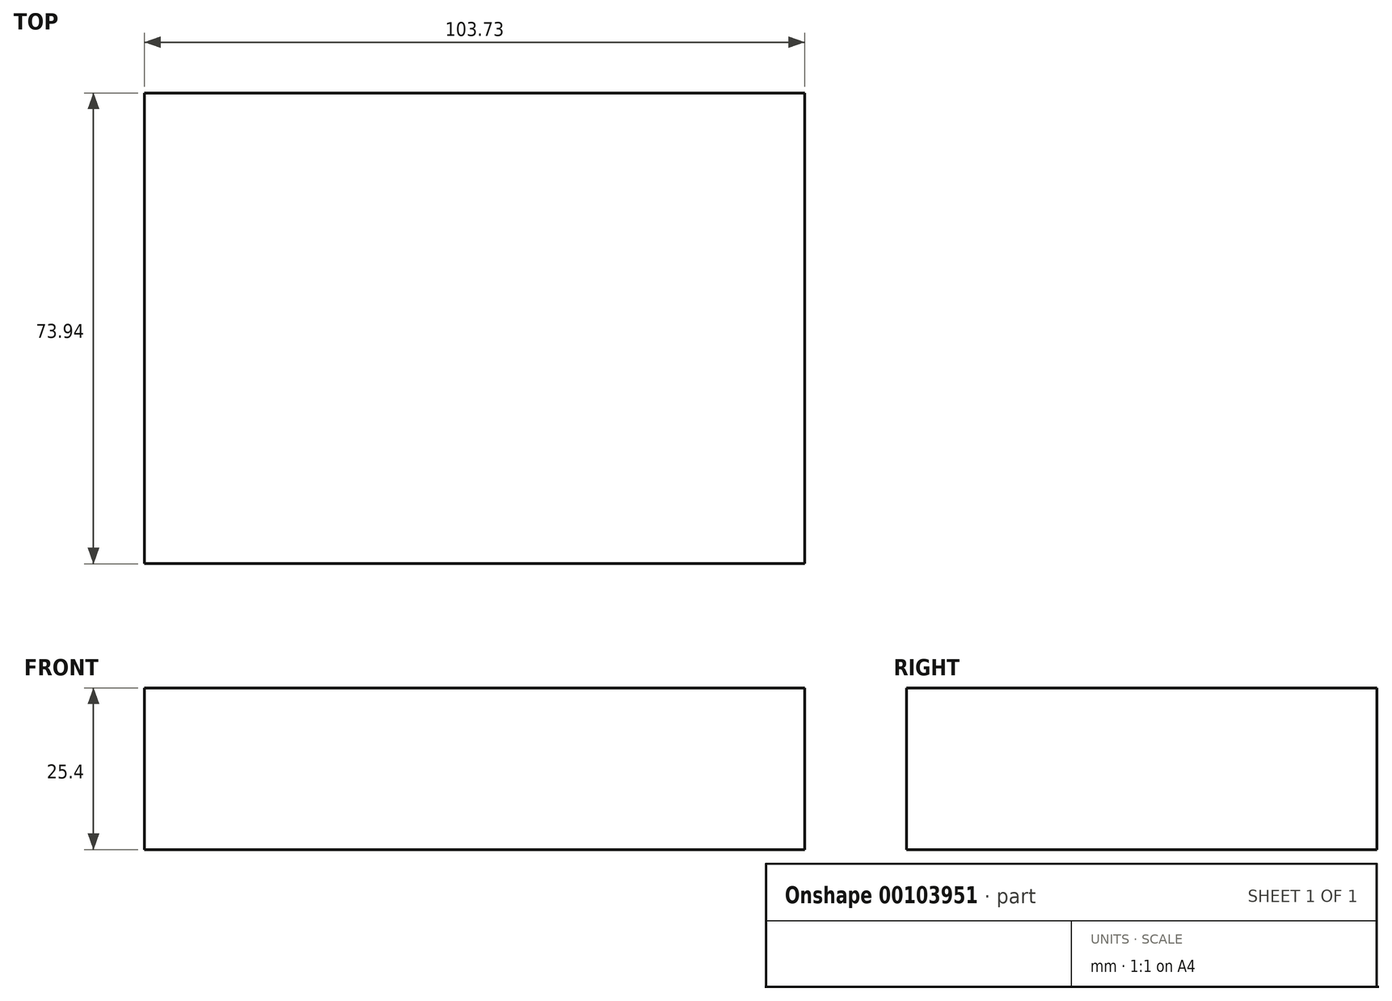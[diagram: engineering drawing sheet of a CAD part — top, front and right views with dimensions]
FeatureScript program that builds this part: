
annotation { "Feature Type Name" : "Feature", "Feature Type Description" : "" }
export const myFeature = defineFeature(function(context is Context, id is Id, definition is map)
    precondition{}
    {
        {
            var Q0;
            Q0=qCreatedBy(makeId("Top.planeOp"),FACE);
            var sketch = newSketch(context, id + "F0", { "sketchPlane" : qUnion([Q0])});
            skLineSegment(sketch, "E0.bottom", {"start": v(-163.34, 17.34) * mm, "end": v(-59.6, 17.34) * mm});
            skLineSegment(sketch, "E0.top", {"start": v(-163.34, -56.6) * mm, "end": v(-59.6, -56.6) * mm});
            skLineSegment(sketch, "E0.left", {"start": v(-163.34, 17.34) * mm, "end": v(-163.34, -56.6) * mm});
            skLineSegment(sketch, "E0.right", {"start": v(-59.6, 17.34) * mm, "end": v(-59.6, -56.6) * mm});
            skSolve(sketch);
        }
        {
            var Q0;
            Q0 = qSketchRegion(id + "F0", true);
            extrude(context, id + "F1", {"entities" : qUnion([Q0]), "depth" : 25.4 * mm});
        }
    });
